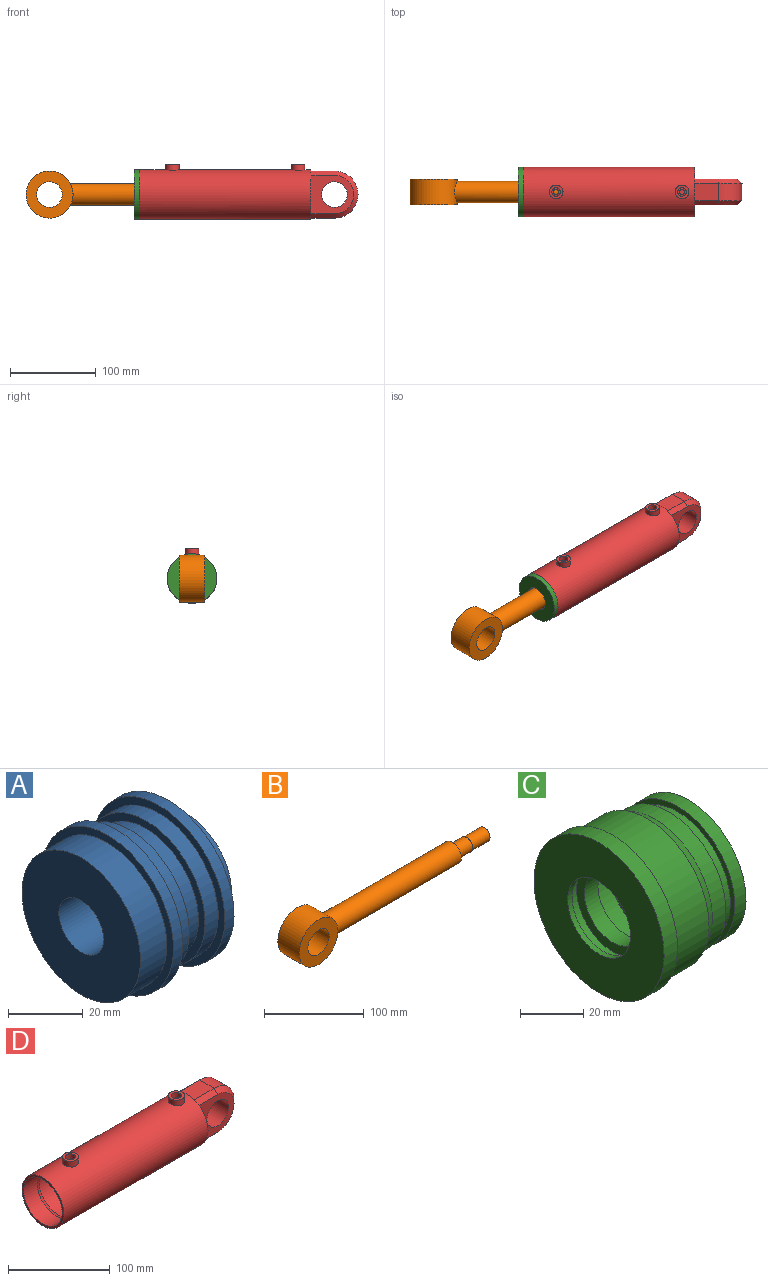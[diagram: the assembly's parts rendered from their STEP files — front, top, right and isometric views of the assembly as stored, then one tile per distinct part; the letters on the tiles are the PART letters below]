
ASSEMBLY  parts=4 mates=3
PART A: 18 faces, bbox 40x50x50 mm
  f0: plane 45x45mm, normal (-1,0,0), area 1363.5mm2, adj f1,f17
  f1: cylinder r=8.5mm len=20mm, axis (-1,0,0), area 1068.1mm2, adj f0,f2
  f2: plane 17x17mm, normal (-1,0,0), area 73mm2, adj f1,f3
  f3: cylinder r=7mm len=20mm, axis (-1,0,0), area 879.6mm2, adj f2,f4
  f4: plane 34x34mm, normal (1,0,0), area 754mm2, adj f3,f5
  f5: cylinder r=17mm len=34mm, axis (-1,0,0), area 747.7mm2, adj f4,f6
  f6: plane 50x50mm, normal (1,0,0), area 1055.6mm2, adj f5,f7
  f7: cylinder r=25mm len=50mm, axis (-1,0,0), area 549.8mm2, adj f6,f8
  f8: plane 50x50mm, normal (-1,0,0), area 373.1mm2, adj f7,f9
  f9: cylinder r=22.5mm len=45mm, axis (-1,0,0), area 706.9mm2, adj f8,f10
  f10: plane 45x45mm, normal (-1,0,0), area 333.8mm2, adj f9,f11
  f11: cylinder r=20mm len=40mm, axis (-1,0,0), area 754mm2, adj f10,f12
  f12: plane 45x45mm, normal (1,0,0), area 333.8mm2, adj f11,f13
  f13: cylinder r=22.5mm len=45mm, axis (-1,0,0), area 706.9mm2, adj f12,f14
  f14: plane 50x50mm, normal (1,0,0), area 373.1mm2, adj f13,f15
  f15: cylinder r=25mm len=50mm, axis (-1,0,0), area 549.8mm2, adj f14,f16
  f16: plane 50x50mm, normal (-1,0,0), area 373.1mm2, adj f15,f17
  f17: cylinder r=22.5mm len=45mm, axis (-1,0,0), area 1413.7mm2, adj f0,f16
PART B: 10 faces, bbox 277.5x30x55 mm
  f0: cylinder r=12.5mm len=180.51mm, axis (-1,0,0), area 14057.1mm2, adj f5,f6
  f1: plane 16x16mm, normal (1,0,0), area 201.1mm2, adj f2
  f2: cylinder r=8mm len=25mm, axis (-1,0,0), area 1256.6mm2, adj f1,f3
  f3: plane 17x17mm, normal (1,0,0), area 25.9mm2, adj f2,f4
  f4: cylinder r=8.5mm len=20mm, axis (-1,0,0), area 1068.1mm2, adj f3,f5
  f5: plane 25x25mm, normal (1,0,0), area 263.9mm2, adj f0,f4
  f6: cylinder r=27.5mm len=55mm, axis (0,1,0), area 4679mm2, adj f0,f8,f9
  f7: cylinder r=15mm len=30mm, axis (0,1,0), area 2827.4mm2, adj f8,f9
  f8: plane 55x55mm, normal (0,-1,0), area 1669mm2, adj f6,f7
  f9: plane 55x55mm, normal (0,1,0), area 1669mm2, adj f6,f7
PART C: 20 faces, bbox 40x58x58 mm
  f0: cylinder r=16mm len=32mm, axis (-1,0,0), area 402.1mm2, adj f1,f19
  f1: plane 32x32mm, normal (-1,0,0), area 313.4mm2, adj f0,f2
  f2: cylinder r=12.5mm len=25mm, axis (-1,0,0), area 471.2mm2, adj f1,f3
  f3: plane 36x36mm, normal (1,0,0), area 527mm2, adj f2,f4
  f4: cylinder r=18mm len=36mm, axis (-1,0,0), area 1131mm2, adj f3,f5
  f5: plane 36x36mm, normal (-1,0,0), area 527mm2, adj f4,f6
  f6: cylinder r=12.5mm len=25mm, axis (-1,0,0), area 1413.7mm2, adj f5,f7
  f7: plane 51x51mm, normal (1,0,0), area 1551.9mm2, adj f6,f8
  f8: cylinder r=25.5mm len=51mm, axis (-1,0,0), area 801.1mm2, adj f7,f9
  f9: plane 51x51mm, normal (-1,0,0), area 307.9mm2, adj f8,f10
  f10: cylinder r=23.5mm len=47mm, axis (-1,0,0), area 590.6mm2, adj f9,f11
  f11: plane 51x51mm, normal (1,0,0), area 307.9mm2, adj f10,f12
  f12: cylinder r=25.5mm len=51mm, axis (-1,0,0), area 961.3mm2, adj f11,f13
  f13: cone r=27.5mm half-angle=30deg, axis (-1,0,0), area 666mm2, adj f12,f14
  f14: cylinder r=27.5mm len=55mm, axis (-1,0,0), area 2684.4mm2, adj f13,f15
  f15: plane 58x58mm, normal (1,0,0), area 266.2mm2, adj f14,f16
  f16: cylinder r=29mm len=58mm, axis (-1,0,0), area 1093.3mm2, adj f15,f17
  f17: plane 58x58mm, normal (-1,0,0), area 2026.3mm2, adj f16,f18
  f18: cylinder r=14mm len=28mm, axis (-1,0,0), area 175.9mm2, adj f17,f19
  f19: plane 32x32mm, normal (1,0,0), area 188.5mm2, adj f0,f18
PART D: 38 faces, bbox 255x58x64 mm
  f0: cylinder r=25mm len=143.63mm, axis (-1,0,0), area 22532.4mm2, adj f11,f12,f37
  f1: cylinder r=29mm len=10mm, axis (-1,0,0), area 50.5mm2, adj f35,f37
  f2: cylinder r=25.5mm len=51mm, axis (-1,0,0), area 3897.2mm2, adj f10,f11,f36
  f3: cylinder r=29mm len=10mm, axis (-1,0,0), area 50.5mm2, adj f32,f36
  f4: cylinder r=29mm len=200mm, axis (-1,0,0), area 36036.9mm2, adj f5,f6,f7,f8,f13,f14,f15,f16
  f5: plane 54.11x18.55mm, normal (1,0,0), area 502.9mm2, adj f4,f23,f27,f29
  f6: plane 18.41x1.5mm, normal (1,0,0), area 18.5mm2, adj f4,f18
  f7: plane 54.11x18.55mm, normal (1,0,0), area 502.9mm2, adj f4,f22,f24,f26
  f8: plane 58x58mm, normal (-1,0,0), area 410.1mm2, adj f4,f9
  f9: cylinder r=26.65mm len=53.31mm, axis (-1,0,0), area 3098.3mm2, adj f8,f10
  f10: cone r=25.5mm half-angle=30deg, axis (-1,0,0), area 378.2mm2, adj f2,f9
  f11: cone r=25mm half-angle=20deg, axis (-1,0,0), area 231.9mm2, adj f0,f2
  f12: plane 50x50mm, normal (-1,0,0), area 1963.5mm2, adj f0
  f13: plane 18.41x1.5mm, normal (1,0,0), area 18.5mm2, adj f4,f21
  f14: plane 1.24x0.45mm, normal (-1,0,0), area 0.2mm2, adj f4,f21,f27
  f15: plane 1.24x0.45mm, normal (-1,0,0), area 0.2mm2, adj f4,f18,f29
  f16: plane 1.24x0.45mm, normal (-1,0,0), area 0.2mm2, adj f4,f18,f26
  f17: plane 1.24x0.45mm, normal (-1,0,0), area 0.2mm2, adj f4,f21,f24
  f18: plane 27.5x20mm, normal (0,0,-1), area 550mm2, adj f6,f15,f16,f19,f26,f29
  f19: cylinder r=27.5mm len=55mm, axis (0,1,0), area 1727.9mm2, adj f18,f21,f25,f28
  f20: cylinder r=15mm len=30mm, axis (0,1,0), area 2827.4mm2, adj f22,f23
  f21: plane 27.5x20mm, normal (0,0,1), area 550mm2, adj f13,f14,f17,f19,f24,f27
  f22: plane 50x45mm, normal (0,-1,0), area 1325.9mm2, adj f7,f20,f24,f25,f26
  f23: plane 50x45mm, normal (0,1,0), area 1325.9mm2, adj f5,f20,f27,f28,f29
  f24: plane 27.5x5mm, normal (0,-0.71,0.71), area 194.5mm2, adj f7,f17,f21,f22,f25
  f25: cone r=22.5mm half-angle=45deg, axis (0,1,0), area 555.4mm2, adj f19,f22,f24,f26
  f26: plane 27.5x5mm, normal (0,-0.71,-0.71), area 194.5mm2, adj f7,f16,f18,f22,f25
  f27: plane 27.5x5mm, normal (0,0.71,0.71), area 194.5mm2, adj f5,f14,f21,f23,f28
  f28: cone r=27.5mm half-angle=45deg, axis (0,-1,0), area 555.4mm2, adj f19,f23,f27,f29
  f29: plane 27.5x5mm, normal (0,0.71,-0.71), area 194.5mm2, adj f5,f15,f18,f23,f28
  f30: plane 16x16mm, normal (0,0,1), area 122.5mm2, adj f31,f32
  f31: cylinder r=8mm len=16mm, axis (0,0,1), area 329.7mm2, adj f4,f30
  f32: cylinder r=5mm len=10mm, axis (0,0,1), area 195.3mm2, adj f3,f30
  f33: plane 16x16mm, normal (0,0,1), area 122.5mm2, adj f34,f35
  f34: cylinder r=8mm len=16mm, axis (0,0,1), area 329.7mm2, adj f4,f33
  f35: cylinder r=5mm len=10mm, axis (0,0,1), area 195.3mm2, adj f1,f33
  f36: cylinder r=3mm len=6mm, axis (0,0,1), area 66.2mm2, adj f2,f3
  f37: cylinder r=3mm len=6mm, axis (0,0,1), area 75.6mm2, adj f0,f1
PLACE A t=(-25.86,27.26,-64.48)mm
PLACE B t=(-25.86,27.26,-64.48)mm
PLACE C rot(axis=(-0.51,-0.42,-0.75),0deg) t=(18.65,27.26,-64.48)mm
PLACE D rot(axis=(-0.51,-0.42,-0.75),0deg) t=(18.65,27.26,-64.48)mm fixed
MATE fastened C.f0 <-> D.f0  axis (1,0,0) through (79.35,27.26,-64.48)mm
MATE cylindrical B.f0 <-> D.f0  axis (-1,0,0) through (88.33,27.26,-64.48)mm
MATE fastened A.f1 <-> B.f0  axis (-1,0,0) through (179.14,27.26,-64.48)mm
